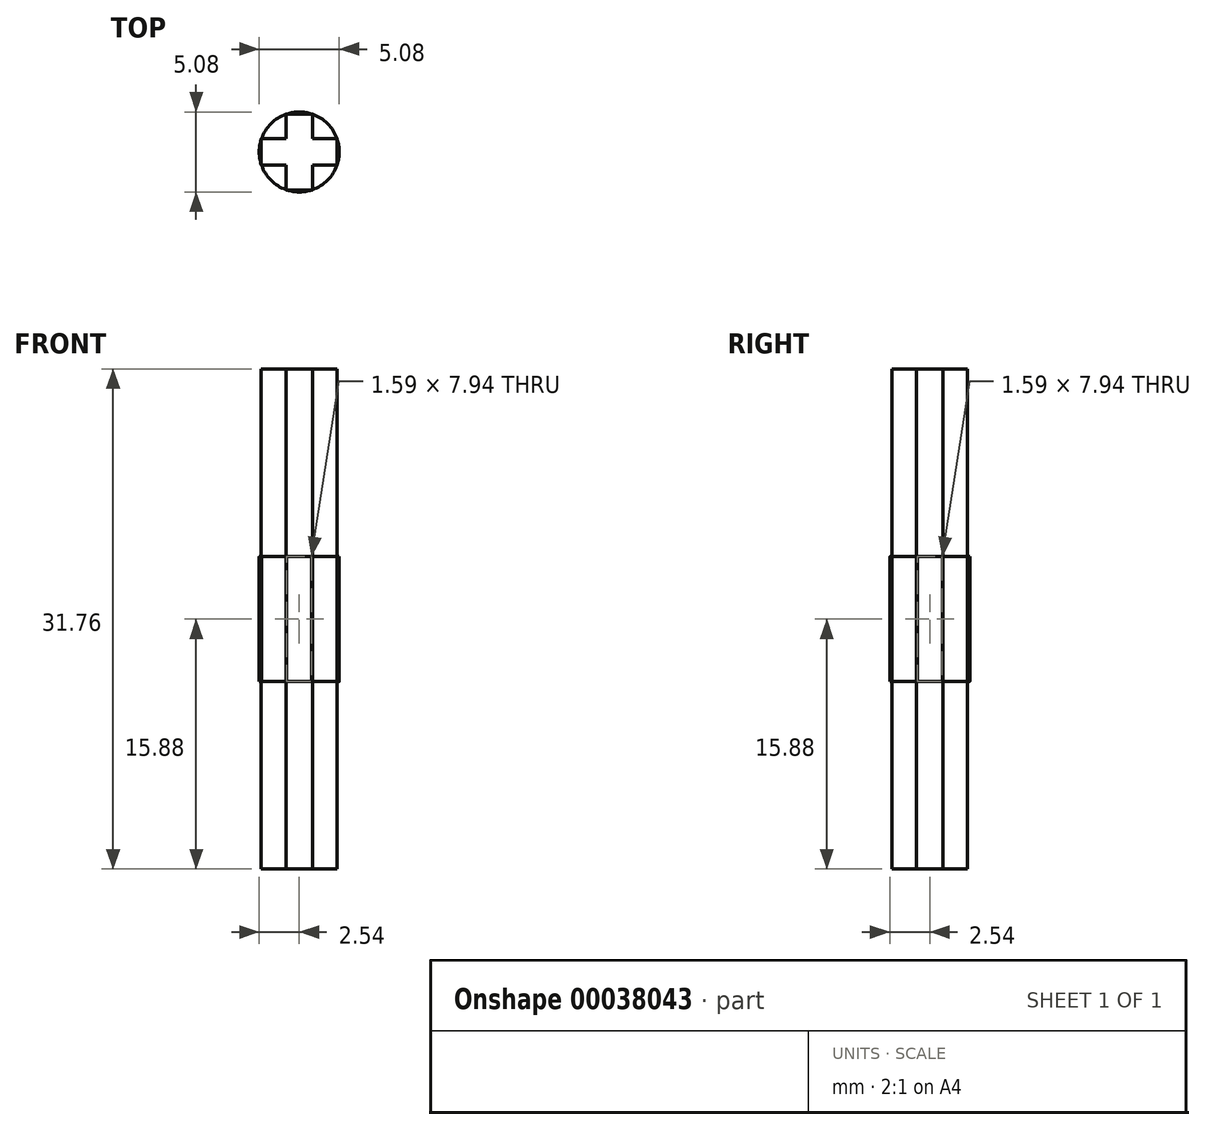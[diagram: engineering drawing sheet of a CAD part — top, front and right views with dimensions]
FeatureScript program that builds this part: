
annotation { "Feature Type Name" : "Feature", "Feature Type Description" : "" }
export const myFeature = defineFeature(function(context is Context, id is Id, definition is map)
    precondition{}
    {
        {
            var Q0;
            Q0=qCreatedBy(makeId("Top.planeOp"),FACE);
            var sketch = newSketch(context, id + "F0", { "sketchPlane" : qUnion([Q0])});
            skLineSegment(sketch, "E0.rect.bottom", {"start": v(0.84, -2.41) * mm, "end": v(-0.84, -2.41) * mm});
            skLineSegment(sketch, "E0.rect.top", {"start": v(0.84, 2.41) * mm, "end": v(-0.84, 2.41) * mm});
            skLineSegment(sketch, "E0.rect.left", {"start": v(0.84, -2.41) * mm, "end": v(0.84, 2.41) * mm});
            skLineSegment(sketch, "E0.rect.right", {"start": v(-0.84, -2.41) * mm, "end": v(-0.84, 2.41) * mm});
            skPoint(sketch, "E0.rect.middle", {"position": v(0, 0) * mm});
            skLineSegment(sketch, "E1.rect.bottom", {"start": v(2.41, -0.84) * mm, "end": v(-2.41, -0.84) * mm});
            skLineSegment(sketch, "E1.rect.top", {"start": v(2.41, 0.84) * mm, "end": v(-2.41, 0.84) * mm});
            skLineSegment(sketch, "E1.rect.left", {"start": v(2.41, -0.84) * mm, "end": v(2.41, 0.84) * mm});
            skLineSegment(sketch, "E1.rect.right", {"start": v(-2.41, -0.84) * mm, "end": v(-2.41, 0.84) * mm});
            skSolve(sketch);
        }
        {
            var Q0;
            Q0=qSketchRegion(id+"F0",true);
            extrude(context, id + "F1", {"entities" : qUnion([Q0]), "endBound" : BoundingType.SYMMETRIC, "depth" : 31.75 * mm});
        }
        {
            var Q0;
            Q0=qCreatedBy(makeId("Top.planeOp"),FACE);
            var sketch = newSketch(context, id + "F2", { "sketchPlane" : qUnion([Q0])});
            skCircle(sketch, "E2", {"center": v(0, 0) * mm, "radius": 2.54 * mm});
            skSolve(sketch);
        }
        {
            var Q0;
            Q0=qSketchRegion(id+"F2",true);
            extrude(context, id + "F3", {"entities" : qUnion([Q0]), "operationType" : NewBodyOperationType.ADD, "endBound" : BoundingType.SYMMETRIC, "depth" : 7.94 * mm});
        }
    });
